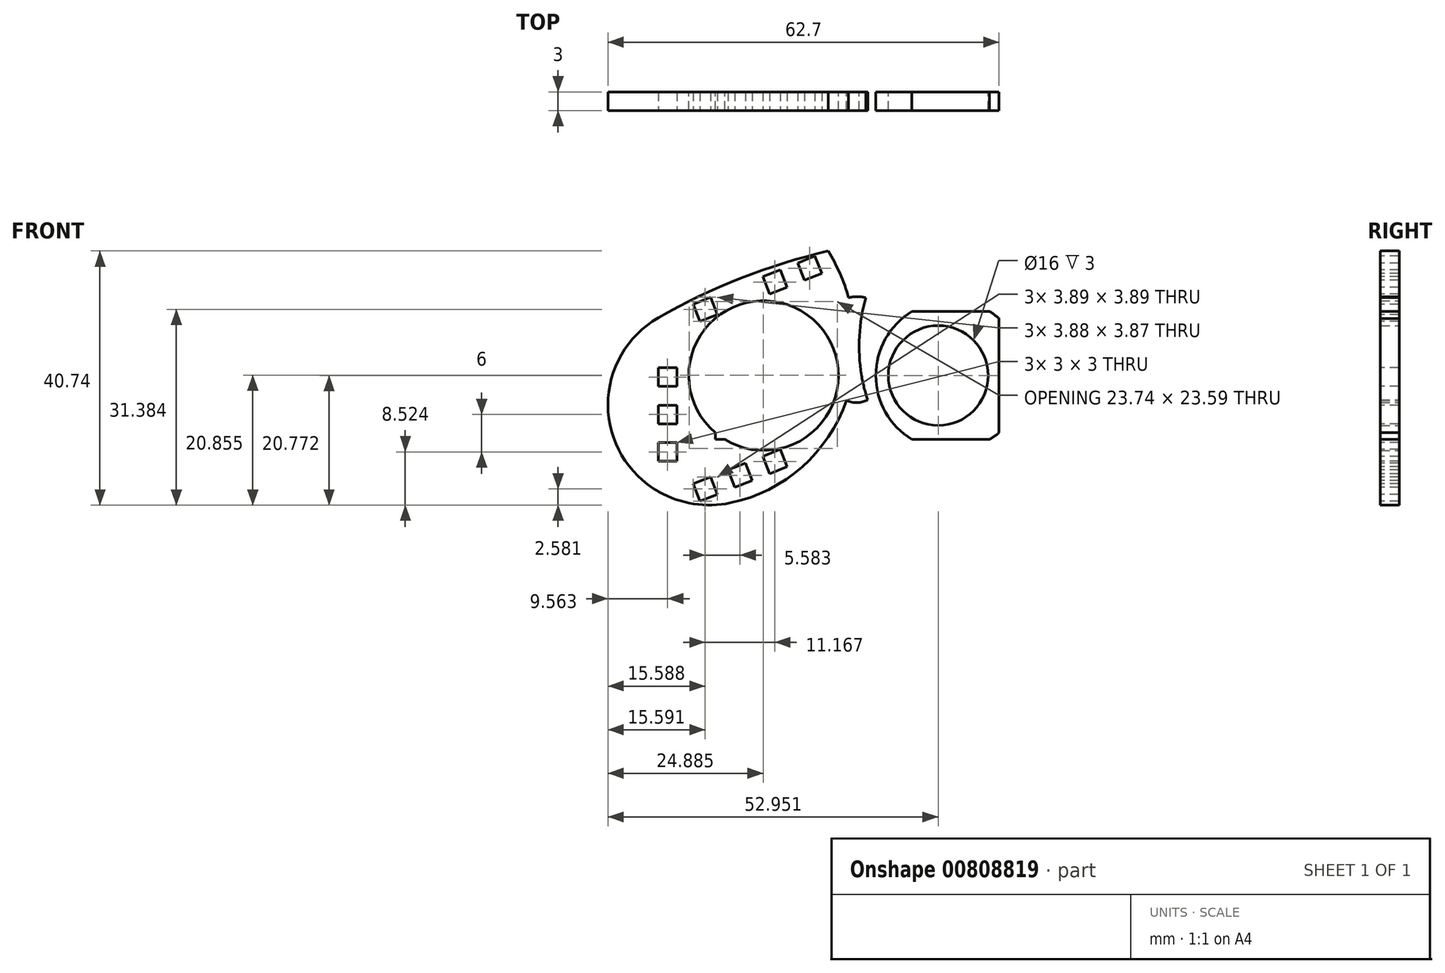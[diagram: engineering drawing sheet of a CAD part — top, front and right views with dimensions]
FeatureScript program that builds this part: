
annotation { "Feature Type Name" : "Feature", "Feature Type Description" : "" }
export const myFeature = defineFeature(function(context is Context, id is Id, definition is map)
    precondition{}
    {
        {
            var Q0;
            Q0=qCreatedBy(makeId("Front.planeOp"),FACE);
            var sketch = newSketch(context, id + "F0", { "sketchPlane" : qUnion([Q0])});
            skCircle(sketch, "E0", {"center": v(-57.26, 21.67) * mm, "radius": 8 * mm});
            skCircle(sketch, "E1", {"center": v(-31.26, 21.67) * mm, "radius": 8 * mm});
            skArc(sketch, "E2", {"start": v(-48.9, 41.64) * mm, "mid": v(-62.92, 37.28) * mm, "end": v(-76.15, 30.92) * mm});
            skArc(sketch, "E3", {"start": v(-76.15, 30.92) * mm, "mid": v(-84.21, 16.95) * mm, "end": v(-76.05, 3.03) * mm});
            skArc(sketch, "E4", {"start": v(-76.05, 3.03) * mm, "mid": v(-76.03, 3.01) * mm, "end": v(-76, 3) * mm});
            skArc(sketch, "E5", {"start": v(-76, 3) * mm, "mid": v(-70.46, 1.1) * mm, "end": v(-64.6, 1.25) * mm});
            skArc(sketch, "E6", {"start": v(-64.6, 1.25) * mm, "mid": v(-51.6, 8.44) * mm, "end": v(-44.96, 21.73) * mm});
            skArc(sketch, "E7", {"start": v(-44.96, 21.73) * mm, "mid": v(-45.13, 32.05) * mm, "end": v(-48.9, 41.64) * mm});
            skCircle(sketch, "E8", {"center": v(-59.26, 21.67) * mm, "radius": 12 * mm});
            skPoint(sketch, "E8.first.point", {"position": v(-71.22, 22.62) * mm});
            skPoint(sketch, "E8.second.point", {"position": v(-47.26, 21.67) * mm});
            skPoint(sketch, "E8.third.point", {"position": v(-54.19, 10.8) * mm});
            skLineSegment(sketch, "E9", {"start": v(-44.26, 32.76) * mm, "end": v(-44.26, 13.54) * mm, "construction": true});
            skArc(sketch, "E10.MirrorCS", {"start": v(-43.56, 21.73) * mm, "mid": v(-43.39, 32.05) * mm, "end": v(-39.6, 41.64) * mm});
            skArc(sketch, "E11.MirrorCS", {"start": v(-23.92, 1.25) * mm, "mid": v(-36.92, 8.44) * mm, "end": v(-43.56, 21.73) * mm});
            skArc(sketch, "E12.MirrorCS", {"start": v(-12.5, 3) * mm, "mid": v(-18.06, 1.1) * mm, "end": v(-23.92, 1.25) * mm});
            skArc(sketch, "E13.MirrorCS", {"start": v(-12.47, 3.03) * mm, "mid": v(-12.49, 3.01) * mm, "end": v(-12.5, 3) * mm});
            skArc(sketch, "E14.MirrorCS", {"start": v(-12.37, 30.92) * mm, "mid": v(-4.3, 16.95) * mm, "end": v(-12.47, 3.03) * mm});
            skArc(sketch, "E15.MirrorCS", {"start": v(-39.6, 41.64) * mm, "mid": v(-25.6, 37.28) * mm, "end": v(-12.37, 30.92) * mm});
            skCircle(sketch, "E16.MirrorC", {"center": v(-29.26, 21.67) * mm, "radius": 12 * mm});
            skArc(sketch, "E17", {"start": v(-45.98, 17.68) * mm, "mid": v(-44.26, 17.32) * mm, "end": v(-42.57, 17.77) * mm});
            skArc(sketch, "E18", {"start": v(-42.88, 34.16) * mm, "mid": v(-44.26, 34.33) * mm, "end": v(-45.64, 34.16) * mm});
            skLineSegment(sketch, "E19", {"start": v(-57.26, 21.67) * mm, "end": v(-31.26, 21.67) * mm});
            skLineSegment(sketch, "E20.bottom", {"start": v(-21.5, 11.42) * mm, "end": v(-67, 11.42) * mm});
            skLineSegment(sketch, "E20.top", {"start": v(-21.5, 31.92) * mm, "end": v(-67, 31.92) * mm});
            skLineSegment(sketch, "E20.left", {"start": v(-21.5, 11.42) * mm, "end": v(-21.5, 31.92) * mm});
            skLineSegment(sketch, "E20.right", {"start": v(-67, 11.42) * mm, "end": v(-67, 31.92) * mm});
            skPoint(sketch, "E20.middle", {"position": v(-44.26, 21.67) * mm});
            skSolve(sketch);
        }
        {
            var Q0;
            Q0=makeQuery(id+"F0.imprint","IMPRINT",FACE,{"disambiguationData":[TD([[makeQuery(id+"F0.imprint","IMPRINT",EDGE,{"derivedFrom":sQuery(id+"F0.wireOp",EDGE,"E2")}),1.0]])]});
            var Q1;
            Q1=makeQuery(id+"F0.imprint","IMPRINT",FACE,{"disambiguationData":[TD([[makeQuery(id+"F0.imprint","IMPRINT",EDGE,{"derivedFrom":sQuery(id+"F0.wireOp",EDGE,"E10.MirrorCS")}),-1.0]])]});
            var Q2;
            {var subQ3=sQuery(id+"F0.wireOp",EDGE,"E17");Q2=makeQuery(id+"F0.imprint","IMPRINT",FACE,{"disambiguationData":[TD([[makeQuery(id+"F0.imprint","IMPRINT",EDGE,{"derivedFrom":subQ3}),1.0]])]});}
            var Q3;
            {var subQ3=sQuery(id+"F0.wireOp",EDGE,"E11.MirrorCS");var subQ7=sQuery(id+"F0.wireOp",EDGE,"E10.MirrorCS");var subQ8=makeQuery(id+"F0.imprint","INTERSECT",VERTEX,{"derivedFrom":[subQ7,subQ3]});Q3=makeQuery(id+"F0.imprint","IMPRINT",FACE,{"disambiguationData":[TD([[makeQuery(id+"F0.imprint","IMPRINT",EDGE,{"disambiguationData":[TD([[subQ8,-1.0]])],"derivedFrom":subQ7}),-1.0]])]});}
            var Q4;
            {var subQ5=sQuery(id+"F0.wireOp",EDGE,"E6");var subQ7=sQuery(id+"F0.wireOp",EDGE,"E7");var subQ8=makeQuery(id+"F0.imprint","INTERSECT",VERTEX,{"derivedFrom":[subQ5,subQ7]});Q4=makeQuery(id+"F0.imprint","IMPRINT",FACE,{"disambiguationData":[TD([[makeQuery(id+"F0.imprint","IMPRINT",EDGE,{"disambiguationData":[TD([[subQ8,1.0]])],"derivedFrom":subQ5}),1.0]])]});}
            var Q5;
            {var subQ3=sQuery(id+"F0.wireOp",EDGE,"E6");var subQ5=makeQuery(id+"F0.imprint","INTERSECT",VERTEX,{"derivedFrom":[subQ3,sQuery(id+"F0.wireOp",EDGE,"E17")]});Q5=makeQuery(id+"F0.imprint","IMPRINT",FACE,{"disambiguationData":[TD([[makeQuery(id+"F0.imprint","IMPRINT",EDGE,{"disambiguationData":[TD([[subQ5,1.0]])],"derivedFrom":subQ3}),1.0]])]});}
            var Q6;
            {var subQ3=sQuery(id+"F0.wireOp",EDGE,"E11.MirrorCS");var subQ7=makeQuery(id+"F0.imprint","INTERSECT",VERTEX,{"derivedFrom":[subQ3,sQuery(id+"F0.wireOp",EDGE,"E17")]});Q6=makeQuery(id+"F0.imprint","IMPRINT",FACE,{"disambiguationData":[TD([[makeQuery(id+"F0.imprint","IMPRINT",EDGE,{"disambiguationData":[TD([[subQ7,1.0]])],"derivedFrom":subQ3}),-1.0]])]});}
            var Q7;
            {var subQ7=sQuery(id+"F0.wireOp",EDGE,"E7");var subQ8=sQuery(id+"F0.wireOp",EDGE,"E6");var subQ9=makeQuery(id+"F0.imprint","INTERSECT",VERTEX,{"derivedFrom":[subQ8,subQ7]});Q7=makeQuery(id+"F0.imprint","IMPRINT",FACE,{"disambiguationData":[TD([[makeQuery(id+"F0.imprint","IMPRINT",EDGE,{"disambiguationData":[TD([[subQ9,1.0]])],"derivedFrom":subQ8}),-1.0]])]});}
            var Q8;
            {var subQ0=sQuery(id+"F0.wireOp",EDGE,"E18");Q8=makeQuery(id+"F0.imprint","IMPRINT",FACE,{"disambiguationData":[TD([[makeQuery(id+"F0.imprint","IMPRINT",EDGE,{"derivedFrom":subQ0}),1.0]])]});}
            var Q9;
            {var subQ0=sQuery(id+"F0.wireOp",EDGE,"E20.right");var subQ1=sQuery(id+"F0.wireOp",EDGE,"E8");var subQ2=makeQuery(id+"F0.imprint","INTERSECT",VERTEX,{"disambiguationData":[OD(1.0)],"derivedFrom":[subQ1,subQ0]});Q9=makeQuery(id+"F0.imprint","IMPRINT",FACE,{"disambiguationData":[TD([[makeQuery(id+"F0.imprint","IMPRINT",EDGE,{"disambiguationData":[TD([[subQ2,-1.0]])],"derivedFrom":subQ1}),-1.0]])]});}
            var Q10;
            {var subQ0=sQuery(id+"F0.wireOp",EDGE,"E20.left");var subQ1=sQuery(id+"F0.wireOp",EDGE,"E16.MirrorC");var subQ2=makeQuery(id+"F0.imprint","INTERSECT",VERTEX,{"disambiguationData":[OD(1.0)],"derivedFrom":[subQ1,subQ0]});Q10=makeQuery(id+"F0.imprint","IMPRINT",FACE,{"disambiguationData":[TD([[makeQuery(id+"F0.imprint","IMPRINT",EDGE,{"disambiguationData":[TD([[subQ2,-1.0]])],"derivedFrom":subQ1}),1.0]])]});}
            var Q11;
            {var subQ0=sQuery(id+"F0.wireOp",EDGE,"E20.top");var subQ1=sQuery(id+"F0.wireOp",EDGE,"E16.MirrorC");var subQ2=makeQuery(id+"F0.imprint","INTERSECT",VERTEX,{"disambiguationData":[OD(1.0)],"derivedFrom":[subQ1,subQ0]});Q11=makeQuery(id+"F0.imprint","IMPRINT",FACE,{"disambiguationData":[TD([[makeQuery(id+"F0.imprint","IMPRINT",EDGE,{"disambiguationData":[TD([[subQ2,-1.0]])],"derivedFrom":subQ1}),1.0]])]});}
            var Q12;
            {var subQ0=sQuery(id+"F0.wireOp",EDGE,"E20.top");var subQ1=sQuery(id+"F0.wireOp",EDGE,"E8");var subQ2=makeQuery(id+"F0.imprint","INTERSECT",VERTEX,{"disambiguationData":[OD(1.0)],"derivedFrom":[subQ1,subQ0]});Q12=makeQuery(id+"F0.imprint","IMPRINT",FACE,{"disambiguationData":[TD([[makeQuery(id+"F0.imprint","IMPRINT",EDGE,{"disambiguationData":[TD([[subQ2,-1.0]])],"derivedFrom":subQ1}),-1.0]])]});}
            extrude(context, id + "F1", {"entities" : qUnion([Q0, Q1, Q2, Q3, Q4, Q5, Q6, Q7, Q8, Q9, Q10, Q11, Q12]), "depth" : 3 * mm, "offsetDistance" : 25 * mm});
        }
        {
            var Q0;
            Q0=makeQuery(id+"F1.opExtrude","CAP_FACE",FACE,{"disambiguationData":[OSD([sQuery(id+"F0.wireOp",EDGE,"E2"),sQuery(id+"F0.wireOp",EDGE,"E3"),sQuery(id+"F0.wireOp",EDGE,"E4"),sQuery(id+"F0.wireOp",EDGE,"E5"),sQuery(id+"F0.wireOp",EDGE,"E6"),sQuery(id+"F0.wireOp",EDGE,"E7"),sQuery(id+"F0.wireOp",EDGE,"E8"),sQuery(id+"F0.wireOp",EDGE,"E10.MirrorCS"),sQuery(id+"F0.wireOp",EDGE,"E11.MirrorCS"),sQuery(id+"F0.wireOp",EDGE,"E12.MirrorCS"),sQuery(id+"F0.wireOp",EDGE,"E13.MirrorCS"),sQuery(id+"F0.wireOp",EDGE,"E14.MirrorCS"),sQuery(id+"F0.wireOp",EDGE,"E15.MirrorCS"),sQuery(id+"F0.wireOp",EDGE,"E16.MirrorC"),sQuery(id+"F0.wireOp",EDGE,"E17"),sQuery(id+"F0.wireOp",EDGE,"E18")])],"isStart":false});
            var sketch = newSketch(context, id + "F2", { "sketchPlane" : qUnion([Q0])});
            skLineSegment(sketch, "E21", {"start": v(-48.9, 41.64) * mm, "end": v(-76.15, 30.92) * mm});
            skLineSegment(sketch, "E22", {"start": v(-39.6, 41.64) * mm, "end": v(-12.37, 30.92) * mm});
            skLineSegment(sketch, "E23", {"start": v(-76.15, 30.92) * mm, "end": v(-75.06, 28.15) * mm});
            skLineSegment(sketch, "E24", {"start": v(-75.06, 28.15) * mm, "end": v(-72.26, 29.25) * mm});
            skLineSegment(sketch, "E25", {"start": v(-72.26, 29.25) * mm, "end": v(-73.36, 32.02) * mm});
            skLineSegment(sketch, "E26.1.0.0", {"start": v(-66.68, 31.45) * mm, "end": v(-67.77, 34.22) * mm});
            skLineSegment(sketch, "E26.1.0.1", {"start": v(-69.47, 30.35) * mm, "end": v(-66.68, 31.45) * mm});
            skLineSegment(sketch, "E26.1.0.2", {"start": v(-70.56, 33.12) * mm, "end": v(-69.47, 30.35) * mm});
            skLineSegment(sketch, "E26.2.0.0", {"start": v(-61.1, 33.64) * mm, "end": v(-62.19, 36.42) * mm});
            skLineSegment(sketch, "E26.2.0.2", {"start": v(-64.98, 35.32) * mm, "end": v(-63.89, 32.55) * mm});
            skLineSegment(sketch, "E26.3.0.0", {"start": v(-55.51, 35.84) * mm, "end": v(-56.6, 38.61) * mm});
            skLineSegment(sketch, "E26.3.0.1", {"start": v(-58.3, 34.74) * mm, "end": v(-55.51, 35.84) * mm});
            skLineSegment(sketch, "E26.3.0.2", {"start": v(-59.4, 37.52) * mm, "end": v(-58.3, 34.74) * mm});
            skLineSegment(sketch, "E26.4.0.0", {"start": v(-49.93, 38.04) * mm, "end": v(-51.02, 40.81) * mm});
            skLineSegment(sketch, "E26.4.0.1", {"start": v(-52.72, 36.94) * mm, "end": v(-49.93, 38.04) * mm});
            skLineSegment(sketch, "E26.4.0.2", {"start": v(-53.81, 39.71) * mm, "end": v(-52.72, 36.94) * mm});
            skLineSegment(sketch, "E26.direction1", {"start": v(-76.15, 30.92) * mm, "end": v(-70.56, 33.12) * mm, "construction": true});
            skLineSegment(sketch, "E27", {"start": v(-44.26, 25.04) * mm, "end": v(-44.26, 34.33) * mm});
            skPoint(sketch, "E27.startSnap0", {"position": v(-44.26, 34.33) * mm});
            skLineSegment(sketch, "E28.MirrorCS", {"start": v(-34.7, 39.71) * mm, "end": v(-35.8, 36.94) * mm});
            skLineSegment(sketch, "E29.MirrorCS", {"start": v(-12.37, 30.92) * mm, "end": v(-17.95, 33.12) * mm, "construction": true});
            skLineSegment(sketch, "E30.MirrorCS", {"start": v(-29.12, 37.52) * mm, "end": v(-30.21, 34.74) * mm});
            skLineSegment(sketch, "E31.MirrorCS", {"start": v(-17.95, 33.12) * mm, "end": v(-19.05, 30.35) * mm});
            skLineSegment(sketch, "E32.MirrorCS", {"start": v(-19.05, 30.35) * mm, "end": v(-21.84, 31.45) * mm});
            skLineSegment(sketch, "E33.MirrorCS", {"start": v(-21.84, 31.45) * mm, "end": v(-20.75, 34.22) * mm});
            skLineSegment(sketch, "E34.MirrorCS", {"start": v(-16.25, 29.25) * mm, "end": v(-15.16, 32.02) * mm});
            skLineSegment(sketch, "E35.MirrorCS", {"start": v(-27.42, 33.64) * mm, "end": v(-26.33, 36.42) * mm});
            skLineSegment(sketch, "E36.MirrorCS", {"start": v(-12.37, 30.92) * mm, "end": v(-13.46, 28.15) * mm});
            skLineSegment(sketch, "E37.MirrorCS", {"start": v(-23.54, 35.32) * mm, "end": v(-24.63, 32.55) * mm});
            skLineSegment(sketch, "E38.MirrorCS", {"start": v(-35.8, 36.94) * mm, "end": v(-38.59, 38.04) * mm});
            skLineSegment(sketch, "E39.MirrorCS", {"start": v(-33, 35.84) * mm, "end": v(-31.91, 38.61) * mm});
            skLineSegment(sketch, "E40.MirrorCS", {"start": v(-30.21, 34.74) * mm, "end": v(-33, 35.84) * mm});
            skLineSegment(sketch, "E41.MirrorCS", {"start": v(-13.46, 28.15) * mm, "end": v(-16.25, 29.25) * mm});
            skLineSegment(sketch, "E42.MirrorCS", {"start": v(-38.59, 38.04) * mm, "end": v(-37.5, 40.81) * mm});
            skLineSegment(sketch, "E43", {"start": v(-62.19, 7.62) * mm, "end": v(-44.26, 14.68) * mm});
            skLineSegment(sketch, "E44", {"start": v(-44.26, 14.68) * mm, "end": v(-12.37, 2.13) * mm});
            skLineSegment(sketch, "E45", {"start": v(-76.15, 30.92) * mm, "end": v(-76.15, 2.13) * mm});
            skLineSegment(sketch, "E46", {"start": v(-12.37, 2.13) * mm, "end": v(-12.37, 30.92) * mm});
            skLineSegment(sketch, "E47", {"start": v(-70.56, 4.33) * mm, "end": v(-69.47, 1.54) * mm});
            skLineSegment(sketch, "E48", {"start": v(-69.47, 1.54) * mm, "end": v(-66.67, 2.63) * mm});
            skLineSegment(sketch, "E49", {"start": v(-66.67, 2.63) * mm, "end": v(-67.77, 5.43) * mm});
            skLineSegment(sketch, "E50.1.0.0", {"start": v(-61.1, 4.83) * mm, "end": v(-62.19, 7.62) * mm});
            skLineSegment(sketch, "E50.1.0.1", {"start": v(-63.88, 3.73) * mm, "end": v(-61.1, 4.83) * mm});
            skLineSegment(sketch, "E50.1.0.2", {"start": v(-64.98, 6.52) * mm, "end": v(-63.88, 3.73) * mm});
            skLineSegment(sketch, "E50.2.0.0", {"start": v(-55.5, 7.03) * mm, "end": v(-56.6, 9.82) * mm});
            skLineSegment(sketch, "E50.2.0.1", {"start": v(-58.3, 5.93) * mm, "end": v(-55.5, 7.03) * mm});
            skLineSegment(sketch, "E50.2.0.2", {"start": v(-59.4, 8.72) * mm, "end": v(-58.3, 5.93) * mm});
            skLineSegment(sketch, "E50.direction1", {"start": v(-70.56, 4.33) * mm, "end": v(-64.98, 6.52) * mm, "construction": true});
            skLineSegment(sketch, "E51", {"start": v(-17.95, 4.33) * mm, "end": v(-19.05, 1.54) * mm});
            skLineSegment(sketch, "E52", {"start": v(-19.05, 1.54) * mm, "end": v(-21.84, 2.63) * mm});
            skLineSegment(sketch, "E53", {"start": v(-21.84, 2.63) * mm, "end": v(-20.75, 5.43) * mm});
            skLineSegment(sketch, "E54.1.0.0", {"start": v(-23.54, 6.52) * mm, "end": v(-24.64, 3.73) * mm});
            skLineSegment(sketch, "E54.1.0.1", {"start": v(-27.43, 4.83) * mm, "end": v(-26.33, 7.62) * mm});
            skLineSegment(sketch, "E54.1.0.2", {"start": v(-24.64, 3.73) * mm, "end": v(-27.43, 4.83) * mm});
            skLineSegment(sketch, "E54.2.0.0", {"start": v(-29.12, 8.72) * mm, "end": v(-30.22, 5.93) * mm});
            skLineSegment(sketch, "E54.2.0.1", {"start": v(-33.01, 7.03) * mm, "end": v(-31.91, 9.82) * mm});
            skLineSegment(sketch, "E54.2.0.2", {"start": v(-30.22, 5.93) * mm, "end": v(-33.01, 7.03) * mm});
            skLineSegment(sketch, "E54.direction1", {"start": v(-17.95, 4.33) * mm, "end": v(-23.54, 6.52) * mm, "construction": true});
            skLineSegment(sketch, "E55.bottom", {"start": v(-76.15, 22.92) * mm, "end": v(-73.15, 22.92) * mm});
            skLineSegment(sketch, "E55.top", {"start": v(-76.15, 19.92) * mm, "end": v(-73.15, 19.92) * mm});
            skLineSegment(sketch, "E55.left", {"start": v(-76.15, 22.92) * mm, "end": v(-76.15, 19.92) * mm});
            skLineSegment(sketch, "E55.right", {"start": v(-73.15, 22.92) * mm, "end": v(-73.15, 19.92) * mm});
            skLineSegment(sketch, "E56.1.0.0", {"start": v(-76.15, 13.92) * mm, "end": v(-73.15, 13.92) * mm});
            skLineSegment(sketch, "E56.1.0.1", {"start": v(-73.15, 16.92) * mm, "end": v(-73.15, 13.92) * mm});
            skLineSegment(sketch, "E56.1.0.2", {"start": v(-76.15, 16.92) * mm, "end": v(-73.15, 16.92) * mm});
            skLineSegment(sketch, "E56.2.0.0", {"start": v(-76.15, 7.92) * mm, "end": v(-73.15, 7.92) * mm});
            skLineSegment(sketch, "E56.2.0.1", {"start": v(-73.15, 10.92) * mm, "end": v(-73.15, 7.92) * mm});
            skLineSegment(sketch, "E56.2.0.2", {"start": v(-76.15, 10.92) * mm, "end": v(-73.15, 10.92) * mm});
            skLineSegment(sketch, "E56.direction1", {"start": v(-76.14, 21.92) * mm, "end": v(-76.14, 15.92) * mm, "construction": true});
            skLineSegment(sketch, "E57.bottom", {"start": v(-12.37, 22.92) * mm, "end": v(-15.37, 22.92) * mm});
            skLineSegment(sketch, "E57.top", {"start": v(-12.37, 19.92) * mm, "end": v(-15.37, 19.92) * mm});
            skLineSegment(sketch, "E57.left", {"start": v(-12.37, 22.92) * mm, "end": v(-12.37, 19.92) * mm});
            skLineSegment(sketch, "E57.right", {"start": v(-15.37, 22.92) * mm, "end": v(-15.37, 19.92) * mm});
            skLineSegment(sketch, "E58.0.1.0", {"start": v(-12.38, 16.92) * mm, "end": v(-12.38, 13.92) * mm});
            skLineSegment(sketch, "E58.0.1.1", {"start": v(-12.38, 16.92) * mm, "end": v(-15.38, 16.92) * mm});
            skLineSegment(sketch, "E58.0.1.2", {"start": v(-12.38, 13.92) * mm, "end": v(-15.38, 13.92) * mm});
            skLineSegment(sketch, "E58.0.1.3", {"start": v(-15.38, 16.92) * mm, "end": v(-15.38, 13.92) * mm});
            skLineSegment(sketch, "E58.0.2.0", {"start": v(-12.39, 10.92) * mm, "end": v(-12.39, 7.92) * mm});
            skLineSegment(sketch, "E58.0.2.1", {"start": v(-12.39, 10.92) * mm, "end": v(-15.39, 10.92) * mm});
            skLineSegment(sketch, "E58.0.2.2", {"start": v(-12.39, 7.92) * mm, "end": v(-15.39, 7.92) * mm});
            skLineSegment(sketch, "E58.0.2.3", {"start": v(-15.39, 10.92) * mm, "end": v(-15.39, 7.92) * mm});
            skLineSegment(sketch, "E58.direction1", {"start": v(-12.37, 22.92) * mm, "end": v(12.63, 22.92) * mm, "construction": true});
            skLineSegment(sketch, "E58.direction2", {"start": v(-12.37, 22.92) * mm, "end": v(-12.38, 16.92) * mm, "construction": true});
            skPoint(sketch, "E59.orphan", {"position": v(-76.15, 13.92) * mm});
            skPoint(sketch, "E60.orphan", {"position": v(-76.15, 10.92) * mm});
            skPoint(sketch, "E61.orphan", {"position": v(-76.15, 7.92) * mm});
            skLineSegment(sketch, "E62", {"start": v(-62.19, 7.62) * mm, "end": v(-64.98, 6.52) * mm});
            skLineSegment(sketch, "E63", {"start": v(-70.56, 4.33) * mm, "end": v(-67.77, 5.43) * mm});
            skLineSegment(sketch, "E64.0", {"start": v(-47.81, 38.85) * mm, "end": v(-75.05, 28.13) * mm});
            skLineSegment(sketch, "E65.0", {"start": v(-73.15, 30.92) * mm, "end": v(-73.15, 2.13) * mm});
            skLineSegment(sketch, "E66.0", {"start": v(-43.16, 17.47) * mm, "end": v(-15.37, 6.53) * mm});
            skLineSegment(sketch, "E67.0", {"start": v(-15.37, 2.13) * mm, "end": v(-15.37, 3.31) * mm});
            skLineSegment(sketch, "E68.0", {"start": v(-40.7, 38.85) * mm, "end": v(-15.37, 28.88) * mm});
            skLineSegment(sketch, "E69.trimOffspring", {"start": v(-12.37, 5.35) * mm, "end": v(-11.27, 4.92) * mm});
            skLineSegment(sketch, "E70.trimOffspring", {"start": v(-15.37, 6.53) * mm, "end": v(-15.37, 28.9) * mm});
            skLineSegment(sketch, "E71", {"start": v(-15.37, 6.53) * mm, "end": v(-16.47, 3.74) * mm});
            skSolve(sketch);
        }
        {
            var Q0;
            {var subQ0=sQuery(id+"F2.wireOp",EDGE,"E47");Q0=makeQuery(id+"F2.imprint","IMPRINT",FACE,{"disambiguationData":[TD([[makeQuery(id+"F2.imprint","IMPRINT",EDGE,{"derivedFrom":subQ0}),1.0]])]});}
            var Q1;
            {var subQ0=sQuery(id+"F2.wireOp",EDGE,"E54.2.0.0");Q1=makeQuery(id+"F2.imprint","IMPRINT",FACE,{"disambiguationData":[TD([[makeQuery(id+"F2.imprint","IMPRINT",EDGE,{"derivedFrom":subQ0}),-1.0]])]});}
            var Q2;
            {var subQ0=sQuery(id+"F2.wireOp",EDGE,"E54.1.0.0");Q2=makeQuery(id+"F2.imprint","IMPRINT",FACE,{"disambiguationData":[TD([[makeQuery(id+"F2.imprint","IMPRINT",EDGE,{"derivedFrom":subQ0}),-1.0]])]});}
            var Q3;
            {var subQ0=sQuery(id+"F2.wireOp",EDGE,"E51");Q3=makeQuery(id+"F2.imprint","IMPRINT",FACE,{"disambiguationData":[TD([[makeQuery(id+"F2.imprint","IMPRINT",EDGE,{"derivedFrom":subQ0}),-1.0]])]});}
            var Q4;
            Q4=makeQuery(id+"F2.imprint","IMPRINT",FACE,{"disambiguationData":[TD([[makeQuery(id+"F2.imprint","IMPRINT",EDGE,{"derivedFrom":sQuery(id+"F2.wireOp",EDGE,"E58.0.2.0")}),-1.0]])]});
            var Q5;
            Q5=makeQuery(id+"F2.imprint","IMPRINT",FACE,{"disambiguationData":[TD([[makeQuery(id+"F2.imprint","IMPRINT",EDGE,{"derivedFrom":sQuery(id+"F2.wireOp",EDGE,"E58.0.1.0")}),-1.0]])]});
            var Q6;
            Q6=makeQuery(id+"F2.imprint","IMPRINT",FACE,{"disambiguationData":[TD([[makeQuery(id+"F2.imprint","IMPRINT",EDGE,{"derivedFrom":sQuery(id+"F2.wireOp",EDGE,"E57.bottom")}),1.0]])]});
            var Q7;
            {var subQ10=sQuery(id+"F2.wireOp",EDGE,"E31.MirrorCS");Q7=makeQuery(id+"F2.imprint","IMPRINT",FACE,{"disambiguationData":[TD([[makeQuery(id+"F2.imprint","IMPRINT",EDGE,{"derivedFrom":subQ10}),-1.0]])]});}
            var Q8;
            {var subQ0=sQuery(id+"F2.wireOp",EDGE,"E30.MirrorCS");Q8=makeQuery(id+"F2.imprint","IMPRINT",FACE,{"disambiguationData":[TD([[makeQuery(id+"F2.imprint","IMPRINT",EDGE,{"derivedFrom":subQ0}),-1.0]])]});}
            var Q9;
            {var subQ0=sQuery(id+"F2.wireOp",EDGE,"E28.MirrorCS");Q9=makeQuery(id+"F2.imprint","IMPRINT",FACE,{"disambiguationData":[TD([[makeQuery(id+"F2.imprint","IMPRINT",EDGE,{"derivedFrom":subQ0}),-1.0]])]});}
            var Q10;
            {var subQ0=sQuery(id+"F2.wireOp",EDGE,"E33.MirrorCS");var subQ1=sQuery(id+"F2.wireOp",EDGE,"E32.MirrorCS");var subQ2=makeQuery(id+"F2.imprint","INTERSECT",VERTEX,{"derivedFrom":[subQ1,subQ0]});Q10=makeQuery(id+"F2.imprint","IMPRINT",FACE,{"disambiguationData":[TD([[makeQuery(id+"F2.imprint","IMPRINT",EDGE,{"disambiguationData":[TD([[subQ2,1.0]])],"derivedFrom":subQ1}),-1.0]])]});}
            var Q11;
            {var subQ0=sQuery(id+"F2.wireOp",EDGE,"E26.1.0.2");Q11=makeQuery(id+"F2.imprint","IMPRINT",FACE,{"disambiguationData":[TD([[makeQuery(id+"F2.imprint","IMPRINT",EDGE,{"derivedFrom":subQ0}),1.0]])]});}
            var Q12;
            {var subQ0=sQuery(id+"F2.wireOp",EDGE,"E26.3.0.0");Q12=makeQuery(id+"F2.imprint","IMPRINT",FACE,{"disambiguationData":[TD([[makeQuery(id+"F2.imprint","IMPRINT",EDGE,{"derivedFrom":subQ0}),1.0]])]});}
            var Q13;
            {var subQ0=sQuery(id+"F2.wireOp",EDGE,"E26.4.0.0");Q13=makeQuery(id+"F2.imprint","IMPRINT",FACE,{"disambiguationData":[TD([[makeQuery(id+"F2.imprint","IMPRINT",EDGE,{"derivedFrom":subQ0}),1.0]])]});}
            var Q14;
            Q14=makeQuery(id+"F2.imprint","IMPRINT",FACE,{"disambiguationData":[TD([[makeQuery(id+"F2.imprint","IMPRINT",EDGE,{"derivedFrom":sQuery(id+"F2.wireOp",EDGE,"E55.bottom")}),-1.0]])]});
            var Q15;
            {var subQ0=sQuery(id+"F2.wireOp",EDGE,"E56.2.0.0");Q15=makeQuery(id+"F2.imprint","IMPRINT",FACE,{"disambiguationData":[TD([[makeQuery(id+"F2.imprint","IMPRINT",EDGE,{"derivedFrom":subQ0}),1.0]])]});}
            var Q16;
            Q16=makeQuery(id+"F2.imprint","IMPRINT",FACE,{"disambiguationData":[TD([[makeQuery(id+"F2.imprint","IMPRINT",EDGE,{"derivedFrom":sQuery(id+"F2.wireOp",EDGE,"E50.1.0.0")}),1.0]])]});
            var Q17;
            {var subQ0=sQuery(id+"F2.wireOp",EDGE,"E50.2.0.0");Q17=makeQuery(id+"F2.imprint","IMPRINT",FACE,{"disambiguationData":[TD([[makeQuery(id+"F2.imprint","IMPRINT",EDGE,{"derivedFrom":subQ0}),1.0]])]});}
            var Q18;
            {var subQ0=sQuery(id+"F2.wireOp",EDGE,"E56.1.0.0");Q18=makeQuery(id+"F2.imprint","IMPRINT",FACE,{"disambiguationData":[TD([[makeQuery(id+"F2.imprint","IMPRINT",EDGE,{"derivedFrom":subQ0}),1.0]])]});}
            extrude(context, id + "F3", {"entities" : qUnion([Q0, Q1, Q2, Q3, Q4, Q5, Q6, Q7, Q8, Q9, Q10, Q11, Q12, Q13, Q14, Q15, Q16, Q17, Q18]), "operationType" : NewBodyOperationType.REMOVE, "oppositeDirection" : true, "depth" : 25 * mm, "offsetDistance" : 25 * mm});
        }
    });
